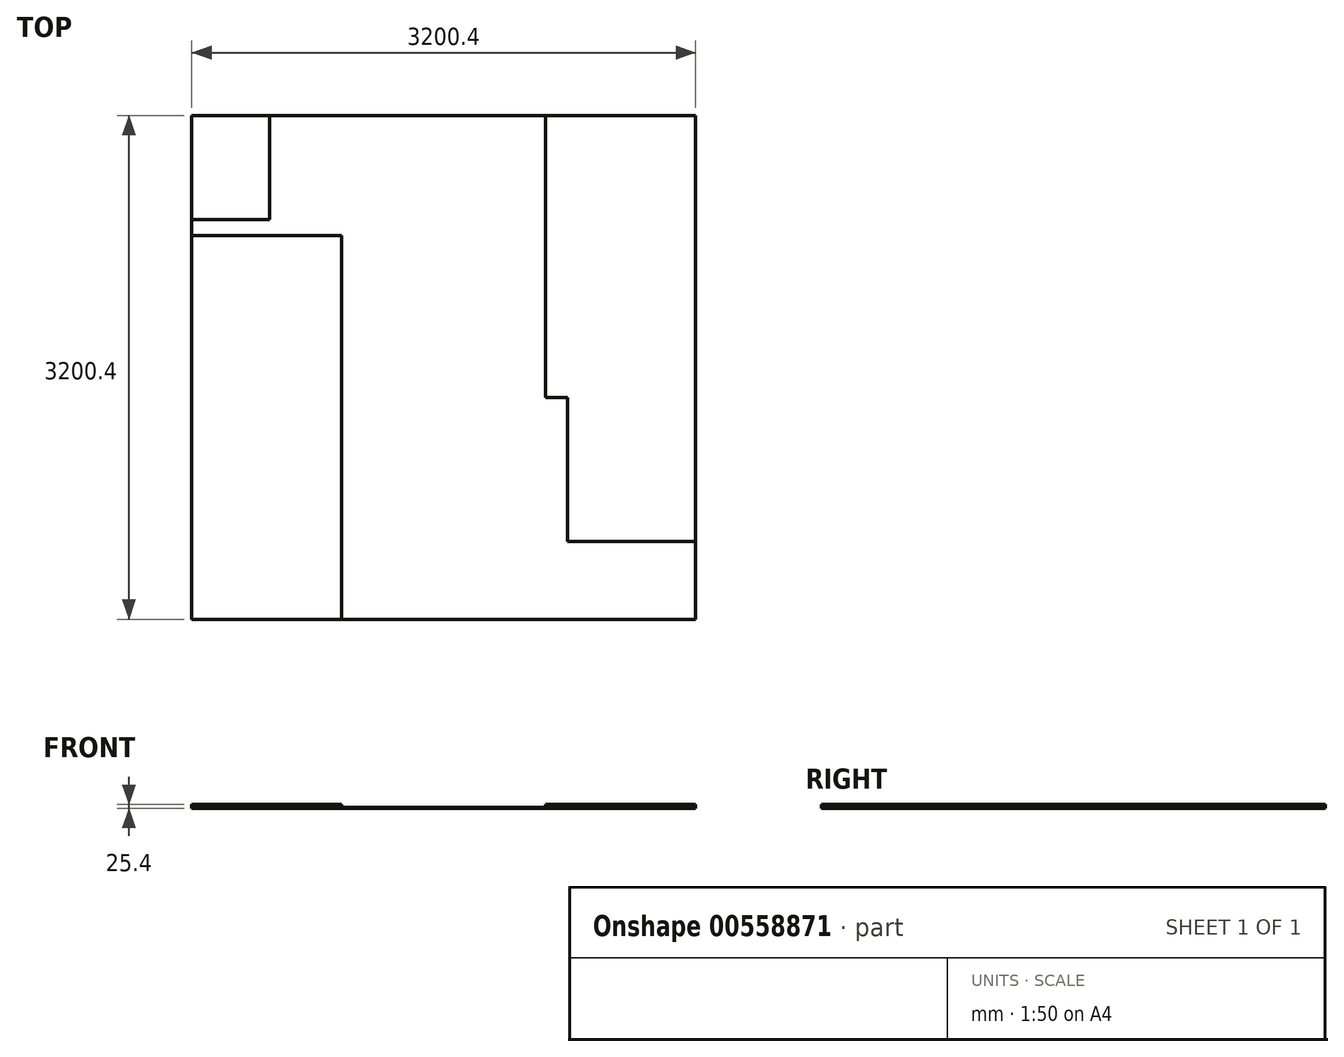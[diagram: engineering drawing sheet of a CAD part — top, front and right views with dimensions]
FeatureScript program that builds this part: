
annotation { "Feature Type Name" : "Feature", "Feature Type Description" : "" }
export const myFeature = defineFeature(function(context is Context, id is Id, definition is map)
    precondition{}
    {
        {
            var Q0;
            Q0=qCreatedBy(makeId("Top.planeOp"),FACE);
            var sketch = newSketch(context, id + "F0", { "sketchPlane" : qUnion([Q0])});
            skLineSegment(sketch, "E0.bottom", {"start": v(-1617.24, 1571.82) * mm, "end": v(1583.16, 1571.82) * mm});
            skLineSegment(sketch, "E0.top", {"start": v(-1617.24, -1628.58) * mm, "end": v(1583.16, -1628.58) * mm});
            skLineSegment(sketch, "E0.left", {"start": v(-1617.24, 1571.82) * mm, "end": v(-1617.24, -1628.58) * mm});
            skLineSegment(sketch, "E0.right", {"start": v(1583.16, 1571.82) * mm, "end": v(1583.16, -1628.58) * mm});
            skSolve(sketch);
        }
        {
            var Q0;
            Q0=makeQuery(id+"F0.imprint","IMPRINT",FACE,{"disambiguationData":[TD([[makeQuery(id+"F0.imprint","IMPRINT",EDGE,{"derivedFrom":sQuery(id+"F0.wireOp",EDGE,"E0.bottom")}),-1.0]])]});
            var sketch = newSketch(context, id + "F1", { "sketchPlane" : qUnion([Q0])});
            skLineSegment(sketch, "E1.bottom", {"start": v(630.66, 1571.82) * mm, "end": v(1583.16, 1571.82) * mm});
            skLineSegment(sketch, "E1.top", {"start": v(630.66, -218.88) * mm, "end": v(1583.16, -218.88) * mm});
            skLineSegment(sketch, "E1.left", {"start": v(630.66, 1571.82) * mm, "end": v(630.66, -218.88) * mm});
            skLineSegment(sketch, "E1.right", {"start": v(1583.16, 1571.82) * mm, "end": v(1583.16, -218.88) * mm});
            skLineSegment(sketch, "E2.bottom", {"start": v(770.36, -218.88) * mm, "end": v(1583.16, -218.88) * mm});
            skLineSegment(sketch, "E2.top", {"start": v(770.36, -1133.28) * mm, "end": v(1583.16, -1133.28) * mm});
            skLineSegment(sketch, "E2.left", {"start": v(770.36, -218.88) * mm, "end": v(770.36, -1133.28) * mm});
            skLineSegment(sketch, "E2.right", {"start": v(1583.16, -218.88) * mm, "end": v(1583.16, -1133.28) * mm});
            skLineSegment(sketch, "E3.bottom", {"start": v(-1617.24, 809.82) * mm, "end": v(-664.74, 809.82) * mm});
            skLineSegment(sketch, "E3.top", {"start": v(-1617.24, -1628.58) * mm, "end": v(-664.74, -1628.58) * mm});
            skLineSegment(sketch, "E3.left", {"start": v(-1617.24, 809.82) * mm, "end": v(-1617.24, -1628.58) * mm});
            skLineSegment(sketch, "E3.right", {"start": v(-664.74, 809.82) * mm, "end": v(-664.74, -1628.58) * mm});
            skLineSegment(sketch, "E4.bottom", {"start": v(-1617.24, 1571.82) * mm, "end": v(-1121.94, 1571.82) * mm});
            skLineSegment(sketch, "E4.top", {"start": v(-1617.24, 911.42) * mm, "end": v(-1121.94, 911.42) * mm});
            skLineSegment(sketch, "E4.left", {"start": v(-1617.24, 1571.82) * mm, "end": v(-1617.24, 911.42) * mm});
            skLineSegment(sketch, "E4.right", {"start": v(-1121.94, 1571.82) * mm, "end": v(-1121.94, 911.42) * mm});
            skSolve(sketch);
        }
        {
            var Q0;
            Q0 = qSketchRegion(id + "F1", true);
            extrude(context, id + "F2", {"entities" : qUnion([Q0]), "depth" : 25.4 * mm, "offsetDistance" : 25.4 * mm});
        }
        {
            var Q0;
            Q0 = qSketchRegion(id + "F0", true);
            extrude(context, id + "F3", {"entities" : qUnion([Q0]), "depth" : 6.35 * mm, "offsetDistance" : 25.4 * mm});
        }
    });
